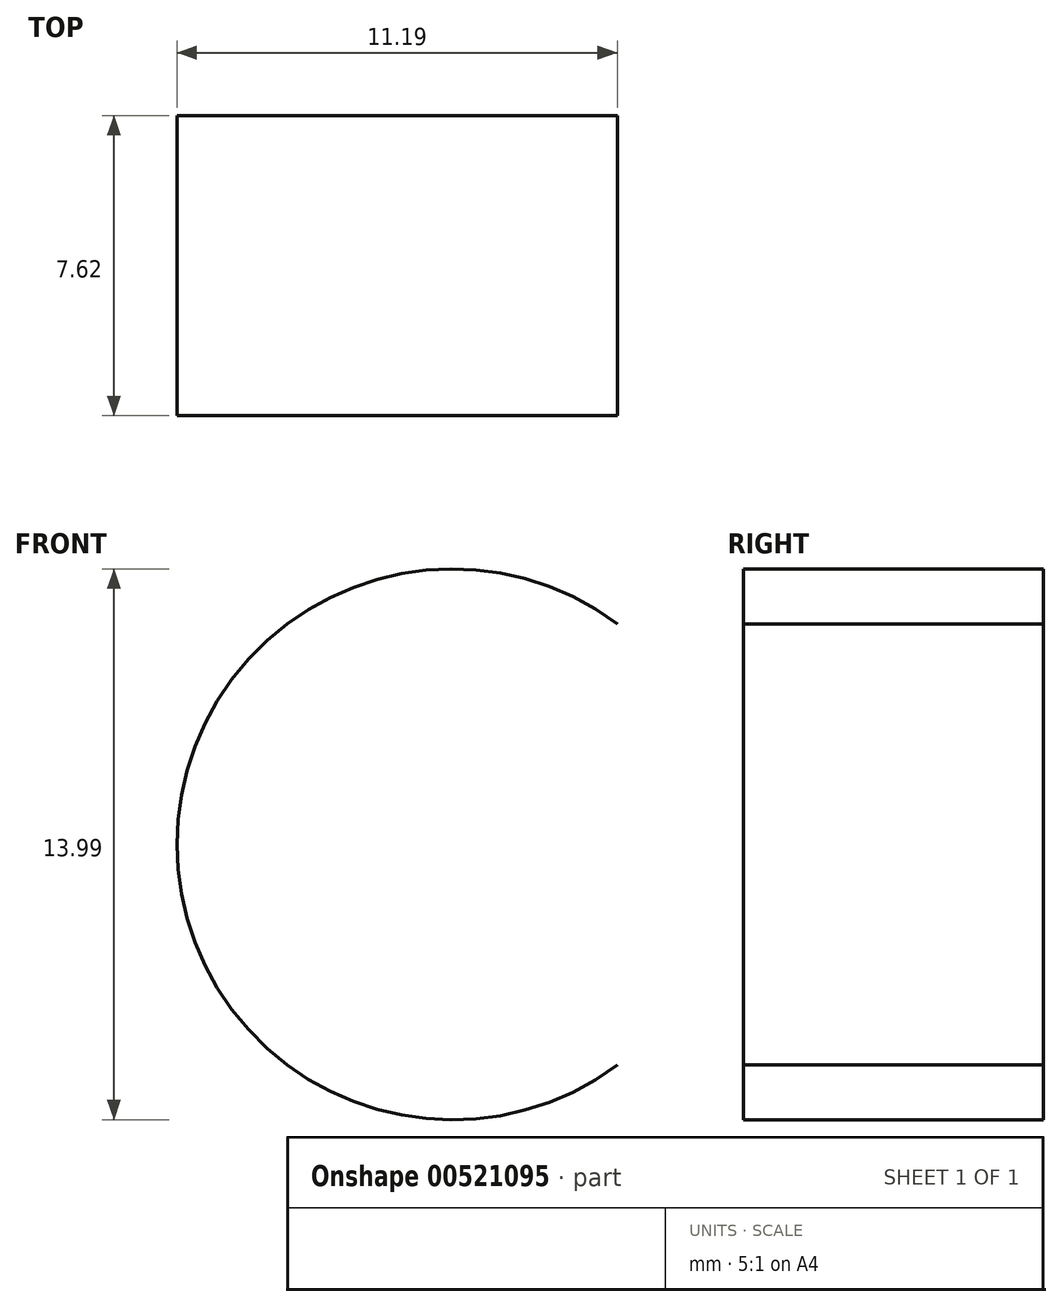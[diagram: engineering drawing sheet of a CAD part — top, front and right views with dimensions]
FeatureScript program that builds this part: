
annotation { "Feature Type Name" : "Feature", "Feature Type Description" : "" }
export const myFeature = defineFeature(function(context is Context, id is Id, definition is map)
    precondition{}
    {
        {
            var Q0;
            Q0=qCreatedBy(makeId("Front.planeOp"),FACE);
            var sketch = newSketch(context, id + "F0", { "sketchPlane" : qUnion([Q0])});
            skCircle(sketch, "E0", {"center": v(0, 0) * mm, "radius": 19.56 * mm});
            skLineSegment(sketch, "E1.bottom", {"start": v(19.56, 0) * mm, "end": v(29.56, 0) * mm});
            skLineSegment(sketch, "E1.top", {"start": v(19.56, 0) * mm, "end": v(29.56, 0) * mm});
            skLineSegment(sketch, "E1.left", {"start": v(19.56, 0) * mm, "end": v(19.56, 0) * mm});
            skLineSegment(sketch, "E1.right", {"start": v(29.56, 0) * mm, "end": v(29.56, 0) * mm});
            skLineSegment(sketch, "E2.top", {"start": v(-29.05, 0) * mm, "end": v(-19.56, 0) * mm});
            skLineSegment(sketch, "E3.bottom", {"start": v(19.56, 0) * mm, "end": v(29.81, 0) * mm});
            skLineSegment(sketch, "E3.top", {"start": v(19.56, 4.33) * mm, "end": v(29.81, 4.33) * mm});
            skLineSegment(sketch, "E3.left", {"start": v(19.56, 0) * mm, "end": v(19.56, 4.33) * mm});
            skLineSegment(sketch, "E3.right", {"start": v(29.81, 0) * mm, "end": v(29.81, 4.33) * mm});
            skLineSegment(sketch, "E4.bottom", {"start": v(-29.05, 0) * mm, "end": v(-19.08, 0) * mm});
            skLineSegment(sketch, "E4.top", {"start": v(-29.05, 4.33) * mm, "end": v(-19.08, 4.33) * mm});
            skLineSegment(sketch, "E4.left", {"start": v(-29.05, 0) * mm, "end": v(-29.05, 4.33) * mm});
            skLineSegment(sketch, "E4.right", {"start": v(-19.08, 0) * mm, "end": v(-19.08, 4.33) * mm});
            skArc(sketch, "E5", {"start": v(40.77, 7.39) * mm, "mid": v(29.58, 1.78) * mm, "end": v(40.77, -3.82) * mm});
            skSolve(sketch);
        }
        {
            var Q0;
            Q0=sQuery(id+"F0.wireOp",EDGE,"E5");
            extrude(context, id + "F1", {"bodyType" : ToolBodyType.SURFACE, "surfaceEntities" : qUnion([Q0]), "endBound" : BoundingType.SYMMETRIC, "depth" : 7.62 * mm, "offsetDistance" : 25.4 * mm});
        }
    });
